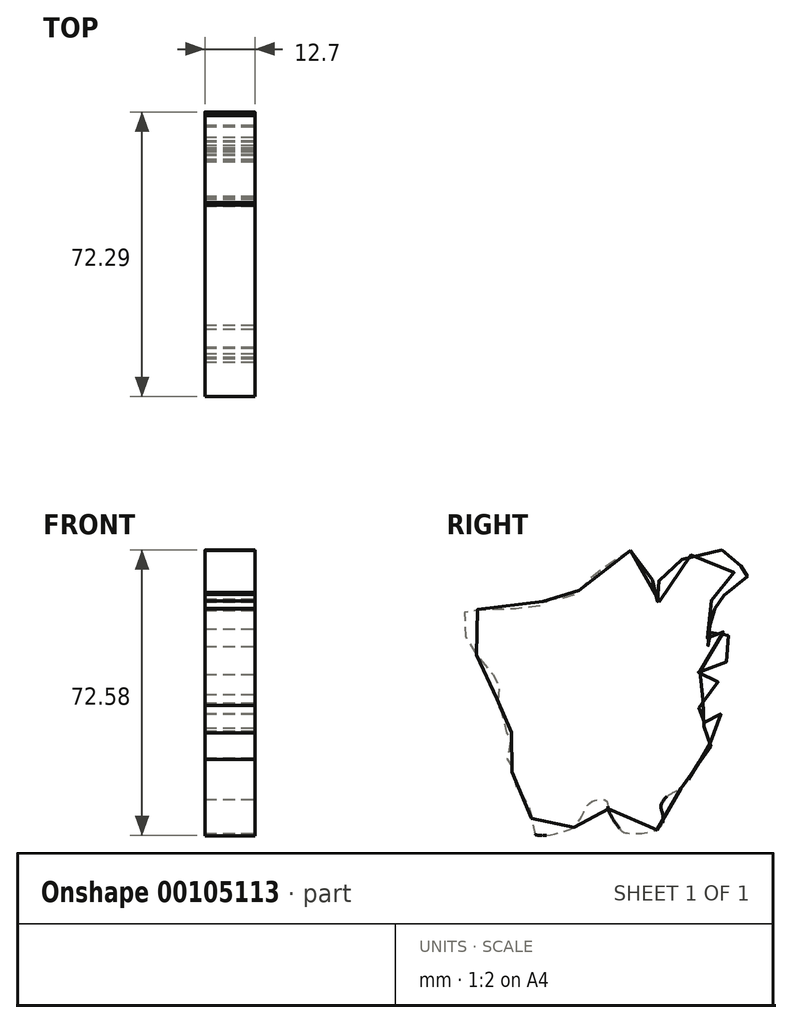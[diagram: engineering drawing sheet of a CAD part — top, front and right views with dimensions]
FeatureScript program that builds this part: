
annotation { "Feature Type Name" : "Feature", "Feature Type Description" : "" }
export const myFeature = defineFeature(function(context is Context, id is Id, definition is map)
    precondition{}
    {
        {
            var Q0;
            Q0=qCreatedBy(makeId("Front.planeOp"),FACE);
            var sketch = newSketch(context, id + "F0", { "sketchPlane" : qUnion([Q0])});
            skLineSegment(sketch, "E0.bottom", {"start": v(38.1, -38.1) * mm, "end": v(-38.1, -38.1) * mm});
            skLineSegment(sketch, "E0.top", {"start": v(38.1, 38.1) * mm, "end": v(-38.1, 38.1) * mm});
            skLineSegment(sketch, "E0.left", {"start": v(38.1, -38.1) * mm, "end": v(38.1, 38.1) * mm});
            skLineSegment(sketch, "E0.right", {"start": v(-38.1, -38.1) * mm, "end": v(-38.1, 38.1) * mm});
            skPoint(sketch, "E0.middle", {"position": v(0, 0) * mm});
            skSolve(sketch);
        }
        {
            var Q0;
            Q0 = qSketchRegion(id + "F0", true);
            extrude(context, id + "F1", {"entities" : qUnion([Q0]), "depth" : 76.2 * mm});
        }
        {
            var Q0;
            Q0=makeQuery(id+"F1.opExtrude","SWEPT_FACE",FACE,{"disambiguationData":[OSD([sQuery(id+"F0.wireOp",EDGE,"E0.right")])]});
            var sketch = newSketch(context, id + "F2", { "sketchPlane" : qUnion([Q0])});
            skFitSpline(sketch, "E1", {"points": [v(30.59, 35.1) * mm, v(34.56, 32.84) * mm, v(38.21, 29.84) * mm, v(41.59, 27.34) * mm, v(44.82, 23.88) * mm, v(45.2, 24.48) * mm, v(48.38, 22.77) * mm, v(48.98, 23.92) * mm, v(51.7, 22.12) * mm, v(53.14, 22.17) * mm, v(54.25, 20.32) * mm, v(60.77, 20.32) * mm, v(69.04, 20.04) * mm, v(72.27, 19.95) * mm, v(73.15, 15.6) * mm, v(71.54, 11.35) * mm, v(69.27, 7.93) * mm, v(65.39, 3.45) * mm, v(63.63, 2.52) * mm, v(64.19, 0) * mm, v(64.51, -2.14) * mm, v(63.9, -4.22) * mm, v(63.26, -3.9) * mm, v(63.54, -8.38) * mm, v(62.2, -11.25) * mm, v(61.18, -10.74) * mm, v(60.72, -12.17) * mm, v(61.78, -13.7) * mm, v(61.78, -17.9) * mm, v(60.67, -17.67) * mm, v(60.81, -18.92) * mm, v(60.35, -22.9) * mm, v(59.01, -26.08) * mm, v(56.51, -29.64) * mm, v(55.13, -31.3) * mm, v(55.82, -33.39) * mm, v(55.73, -36.3) * mm, v(53.05, -37.36) * mm, v(47.46, -36.3) * mm, v(44.5, -34.77) * mm, v(41.96, -30.43) * mm, v(39.74, -28.44) * mm, v(36.69, -28.49) * mm, v(36.22, -30.66) * mm, v(33.68, -35.14) * mm, v(32.2, -36.53) * mm, v(27.44, -36.71) * mm, v(23.1, -35.33) * mm, v(22.36, -32.23) * mm, v(22.82, -29.92) * mm, v(21.16, -27.29) * mm, v(17.55, -25.16) * mm, v(15.38, -21.83) * mm, v(14.6, -19.3) * mm, v(13.8, -19.1) * mm, v(10.02, -15.18) * mm, v(10.48, -14.2) * mm, v(8.12, -10.5) * mm, v(7.75, -6.44) * mm, v(11.82, -10) * mm, v(11.68, -8.2) * mm, v(12.38, -6.35) * mm, v(13.35, -6.26) * mm, v(12.98, -2.98) * mm, v(13.53, -1.45) * mm, v(10.94, -3.62) * mm, v(8.36, -0.94) * mm, v(9.6, 3.26) * mm, v(13.49, 3.73) * mm, v(12.24, 4.74) * mm, v(7.06, 6.13) * mm, v(4.7, 10.1) * mm, v(5.72, 13.43) * mm, v(9.14, 15.14) * mm, v(10.39, 14.63) * mm, v(9.51, 13.3) * mm, v(9.79, 11.12) * mm, v(10.8, 10.75) * mm, v(11.04, 13.06) * mm, v(10.76, 15.93) * mm, v(9.6, 16.48) * mm, v(8.5, 18.52) * mm, v(9.23, 20.5) * mm, v(10.16, 22.21) * mm, v(7.57, 23.5) * mm, v(2.72, 25.77) * mm, v(1.15, 28.87) * mm, v(4.29, 29.47) * mm, v(1.98, 31.87) * mm, v(3.78, 34.46) * mm, v(12.42, 34.74) * mm, v(19.26, 31.78) * mm, v(22.91, 28.22) * mm, v(23.88, 24.39) * mm, v(23.2, 22.17) * mm, v(24.72, 22.58) * mm, v(24.62, 23.78) * mm, v(26.01, 30.35) * mm, v(30.59, 35.1) * mm]});
            skSolve(sketch);
        }
        {
            var Q0;
            Q0 = qSketchRegion(id + "F2", true);
            extrude(context, id + "F3", {"entities" : qUnion([Q0]), "operationType" : NewBodyOperationType.ADD, "depth" : 12.7 * mm});
        }
        {
            var Q0;
            Q0=makeQuery(id+"F1.opExtrude","CAP_FACE",FACE,{"disambiguationData":[OSD([sQuery(id+"F0.wireOp",EDGE,"E0.bottom"),sQuery(id+"F0.wireOp",EDGE,"E0.top"),sQuery(id+"F0.wireOp",EDGE,"E0.left"),sQuery(id+"F0.wireOp",EDGE,"E0.right")])],"isStart":true});
            var sketch = newSketch(context, id + "F4", { "sketchPlane" : qUnion([Q0])});
            skSolve(sketch);
        }
        {
            var Q0;
            Q0=makeQuery(id+"F4.imprint","IMPRINT",FACE,{"disambiguationData":[TD([[makeQuery(id+"F4.imprint","IMPRINT",EDGE,{"derivedFrom":makeQuery(id+"F1.opExtrude","CAP_EDGE",EDGE,{"disambiguationData":[OSD([sQuery(id+"F0.wireOp",EDGE,"E0.bottom")])],"isStart":true})}),1.0]])]});
            extrude(context, id + "F5", {"entities" : qUnion([Q0]), "operationType" : NewBodyOperationType.REMOVE, "oppositeDirection" : true, "depth" : 108.7 * mm});
        }
        {
            var Q0;
            Q0=makeQuery(id+"F3.opExtrude","CAP_FACE",FACE,{"disambiguationData":[OSD([sQuery(id+"F2.wireOp",EDGE,"E1")])],"isStart":false});
            var sketch = newSketch(context, id + "F6", { "sketchPlane" : qUnion([Q0])});
            skFitSpline(sketch, "E2", {"points": [v(26.42, 15.04) * mm, v(26, 17.26) * mm, v(25.8, 20.56) * mm, v(25.92, 24.06) * mm, v(27.03, 27.97) * mm, v(28.72, 31.51) * mm, v(29.71, 32.75) * mm, v(29.46, 31.68) * mm, v(28.19, 29.12) * mm, v(27.57, 26.86) * mm, v(27.16, 24.55) * mm, v(26.91, 20.19) * mm, v(27.2, 15.99) * mm, v(27.32, 14.14) * mm, v(26.42, 15.04) * mm]});
            skFitSpline(sketch, "E3", {"points": [v(28.68, 21.1) * mm, v(28.35, 19.9) * mm, v(28.6, 18.13) * mm, v(29.71, 17.51) * mm, v(29.5, 17.96) * mm, v(29.13, 18.75) * mm, v(28.68, 21.1) * mm]});
            skFitSpline(sketch, "E4", {"points": [v(30.04, 18.87) * mm, v(30.53, 19.12) * mm, v(30.74, 18.46) * mm, v(30.04, 18.87) * mm]});
            skFitSpline(sketch, "E5", {"points": [v(30.99, 19.65) * mm, v(31.81, 19.57) * mm, v(31.77, 19.12) * mm, v(30.99, 19.65) * mm]});
            skFitSpline(sketch, "E6", {"points": [v(31.52, 20.8) * mm, v(32.3, 20.85) * mm, v(32.84, 20.02) * mm, v(32.96, 18.87) * mm, v(32.35, 19.16) * mm, v(31.52, 20.8) * mm]});
            skFitSpline(sketch, "E7", {"points": [v(32.55, 27.02) * mm, v(33.21, 24.22) * mm, v(33.33, 22) * mm, v(33.21, 20.1) * mm, v(33.87, 20.8) * mm, v(34.12, 23.69) * mm, v(33.62, 26.08) * mm, v(32.55, 27.02) * mm]});
            skFitSpline(sketch, "E8", {"points": [v(30.53, 33.49) * mm, v(33.83, 31.63) * mm, v(37.9, 28.3) * mm, v(37.74, 28.83) * mm, v(40.3, 26.82) * mm, v(43.46, 23.65) * mm, v(44.66, 22.45) * mm, v(45.77, 22.2) * mm, v(49.56, 20.44) * mm, v(50.1, 20.1) * mm, v(49.93, 20.52) * mm, v(51.16, 20.19) * mm, v(51.74, 19.57) * mm, v(51.99, 20.06) * mm, v(52.93, 19.57) * mm, v(53.43, 18.09) * mm, v(53.92, 18.3) * mm, v(56.4, 18.66) * mm, v(58.41, 18.58) * mm, v(58.95, 18.75) * mm, v(62.57, 19.28) * mm, v(66.4, 19.28) * mm, v(69.53, 19.12) * mm, v(69.2, 18.7) * mm, v(70.4, 18.7) * mm, v(70.72, 19.28) * mm, v(70.84, 18.46) * mm, v(71.87, 17.76) * mm, v(71.7, 15.82) * mm, v(70.97, 13.35) * mm, v(69.44, 10.47) * mm, v(67.6, 7.26) * mm, v(64.92, 4.5) * mm, v(62.36, 2.77) * mm, v(61.79, 3.27) * mm, v(62, 3.8) * mm, v(65.78, 7.14) * mm, v(68.37, 11.17) * mm, v(70.27, 16.07) * mm, v(70.19, 17.64) * mm, v(66.4, 17.72) * mm, v(61.5, 17.51) * mm, v(56.6, 16.9) * mm, v(54.21, 16.6) * mm, v(54.83, 17.35) * mm, v(55, 17.55) * mm, v(53.06, 17.39) * mm, v(52.48, 18.62) * mm, v(51.9, 17.84) * mm, v(51.08, 18.3) * mm, v(50.75, 18.95) * mm, v(48.49, 20.27) * mm, v(45.9, 21.34) * mm, v(45.73, 20.85) * mm, v(44.37, 21.59) * mm, v(42.76, 23.15) * mm, v(41.12, 23.85) * mm, v(37.9, 26.78) * mm, v(35.31, 29.04) * mm, v(32.68, 31.02) * mm, v(30.53, 33.49) * mm]});
            skFitSpline(sketch, "E9", {"points": [v(60.26, 8.37) * mm, v(60.06, 10.22) * mm, v(61.2, 12.45) * mm, v(64.05, 13.93) * mm, v(66.15, 14.71) * mm, v(68.05, 14.67) * mm, v(66.69, 14.22) * mm, v(63.15, 12.4) * mm, v(61.25, 10.6) * mm, v(60.26, 8.37) * mm]});
            skFitSpline(sketch, "E10", {"points": [v(61.09, 8.58) * mm, v(62.03, 8.87) * mm, v(62.28, 8.5) * mm, v(61.95, 8.08) * mm, v(62.24, 7.8) * mm, v(61.75, 7.05) * mm, v(62.12, 6.72) * mm, v(60.84, 6.64) * mm, v(61.13, 6.85) * mm, v(61.42, 7.3) * mm, v(61.09, 7.75) * mm, v(61.42, 7.84) * mm, v(61.09, 8.58) * mm]});
            skFitSpline(sketch, "E11", {"points": [v(61.79, 2.44) * mm, v(62.45, 1.5) * mm, v(62.73, -0.6) * mm, v(62.9, -2.91) * mm, v(62.36, -2.58) * mm, v(62.2, -3.08) * mm, v(62.12, -4.15) * mm, v(62.28, -6.37) * mm, v(62.24, -8.18) * mm, v(61.79, -9.66) * mm, v(61.79, -8.26) * mm, v(61.37, -5.96) * mm, v(61, -6.95) * mm, v(61.05, -9.09) * mm, v(60.47, -10.98) * mm, v(60.02, -10.53) * mm, v(59.32, -11.43) * mm, v(59.65, -9.38) * mm, v(60.1, -8.6) * mm, v(60.26, -9.17) * mm, v(60.26, -8.02) * mm, v(60.6, -7.03) * mm, v(61.09, -5.34) * mm, v(61.79, -2.25) * mm, v(61.79, 2.44) * mm]});
            skFitSpline(sketch, "E12", {"points": [v(58.53, -10.86) * mm, v(58.62, -11.85) * mm, v(57.8, -12.1) * mm, v(58.29, -11.48) * mm, v(56.56, -12.59) * mm, v(54.05, -13.5) * mm, v(52.56, -13.7) * mm, v(52.15, -14.15) * mm, v(51.04, -14.23) * mm, v(51.37, -13.7) * mm, v(51.12, -13.53) * mm, v(53.14, -13.08) * mm, v(55.82, -12.67) * mm, v(58.53, -10.86) * mm]});
            skFitSpline(sketch, "E13", {"points": [v(46.55, -14.52) * mm, v(49.4, -14.2) * mm, v(49.76, -13.78) * mm, v(50.26, -13.7) * mm, v(50.67, -13.9) * mm, v(50.18, -14.28) * mm, v(49.89, -14.23) * mm, v(49.31, -14.77) * mm, v(46.55, -14.52) * mm]});
            skFitSpline(sketch, "E14", {"points": [v(45.2, -13.29) * mm, v(45.11, -14.2) * mm, v(43.88, -15.8) * mm, v(41.61, -16.3) * mm, v(38.65, -16.42) * mm, v(36.5, -15.72) * mm, v(34.28, -15.22) * mm, v(32.35, -14.4) * mm, v(29.96, -11.97) * mm, v(29.05, -10.03) * mm, v(28.97, -8.92) * mm, v(29.67, -8.39) * mm, v(29.34, -7.11) * mm, v(29.55, -6.66) * mm, v(29.8, -7.6) * mm, v(29.83, -9.54) * mm, v(30.74, -11.31) * mm, v(32.72, -13.25) * mm, v(35.15, -14.6) * mm, v(38.36, -15.47) * mm, v(41.61, -15.51) * mm, v(44.33, -14.52) * mm, v(45.2, -13.29) * mm]});
            skFitSpline(sketch, "E15", {"points": [v(33.91, -11.15) * mm, v(34.82, -10.7) * mm, v(36.8, -10.98) * mm, v(38.9, -11.8) * mm, v(39.51, -12.55) * mm, v(39.35, -13.62) * mm, v(37.78, -13.82) * mm, v(34.86, -12.59) * mm, v(34.03, -11.8) * mm, v(33.91, -11.15) * mm]});
            skFitSpline(sketch, "E16", {"points": [v(33.13, -1.76) * mm, v(33.91, -0.9) * mm, v(34.24, 0.96) * mm, v(34.2, 3.27) * mm, v(33.13, 5.28) * mm, v(31.85, 6.23) * mm, v(29.01, 6.6) * mm, v(27.7, 5.94) * mm, v(27.86, 5.04) * mm, v(27.98, 2.77) * mm, v(28.8, 0) * mm, v(30.78, -0.98) * mm, v(32.6, -1.02) * mm, v(32.6, -1.63) * mm, v(33.13, -1.76) * mm]});
            skFitSpline(sketch, "E17", {"points": [v(47.62, -7.48) * mm, v(47.54, -5.75) * mm, v(48.45, -3.7) * mm, v(50.71, -2.38) * mm, v(53.14, -1.68) * mm, v(55.12, -2.58) * mm, v(55.4, -3.24) * mm, v(55.16, -4.4) * mm, v(53.39, -7.2) * mm, v(50.01, -8.26) * mm, v(48, -7.11) * mm, v(47.62, -7.48) * mm]});
            skFitSpline(sketch, "E18", {"points": [v(31.11, 7.88) * mm, v(29.01, 9.77) * mm, v(27.16, 9.85) * mm, v(26.3, 8.37) * mm, v(25.68, 5.24) * mm, v(25.96, 1.82) * mm, v(27.65, -1.3) * mm, v(30.66, -3.36) * mm, v(31.9, -4.19) * mm, v(31.81, -5.18) * mm, v(33.09, -3.45) * mm, v(32.43, -2.46) * mm, v(29.96, -1.8) * mm, v(27.98, -0.44) * mm, v(27.36, 1.66) * mm, v(27.12, 4.67) * mm, v(27.03, 6.52) * mm, v(28.56, 7.3) * mm, v(31.44, 7.26) * mm, v(31.11, 7.88) * mm]});
            skFitSpline(sketch, "E19", {"points": [v(53.67, -0.85) * mm, v(56.52, 0) * mm, v(59.07, -0.81) * mm, v(58.33, -2.87) * mm, v(56.93, -6.41) * mm, v(53.35, -9.62) * mm, v(48, -10.4) * mm, v(46.26, -10.61) * mm, v(46.22, -8.14) * mm, v(47.42, -8.26) * mm, v(47.3, -9) * mm, v(50.38, -9.3) * mm, v(54.05, -8.06) * mm, v(56.02, -5.34) * mm, v(56.43, -2.79) * mm, v(55.82, -1.76) * mm, v(53.67, -0.85) * mm]});
            skFitSpline(sketch, "E20", {"points": [v(37.25, -9.95) * mm, v(38.93, -10.53) * mm, v(41, -6.37) * mm, v(42.68, -3.24) * mm, v(45.9, -1.3) * mm, v(48.9, 1.58) * mm, v(50.59, 6.89) * mm, v(49.72, 12.2) * mm, v(48.65, 15.37) * mm, v(48.49, 18.42) * mm, v(46.88, 19.16) * mm, v(45.48, 16.81) * mm, v(41.4, 14.26) * mm, v(38.9, 10.18) * mm, v(37.86, 5.65) * mm, v(38.32, 0.34) * mm, v(39.06, -2.79) * mm, v(38.15, -5.18) * mm, v(37.25, -9.95) * mm]});
            skFitSpline(sketch, "E21", {"points": [v(46.63, 14.55) * mm, v(43.26, 12.28) * mm, v(40.33, 7.71) * mm, v(40.13, 1.82) * mm, v(41, -1.14) * mm, v(41.7, -1.06) * mm, v(45.73, 0.8) * mm, v(47.75, 4.83) * mm, v(47.87, 10.84) * mm, v(46.63, 14.55) * mm]});
            skFitSpline(sketch, "E22", {"points": [v(28.29, -9.94) * mm, v(28.45, -8.92) * mm, v(26.1, -6.37) * mm, v(24.75, -5.08) * mm, v(25.28, -6.37) * mm, v(27.1, -9.57) * mm, v(28.29, -9.94) * mm]});
            skFitSpline(sketch, "E23", {"points": [v(25.94, -5.24) * mm, v(25.53, -4.96) * mm, v(25.2, -3.93) * mm, v(25.28, -3.52) * mm, v(25.9, -4.05) * mm, v(25.94, -5.24) * mm]});
            skFitSpline(sketch, "E24", {"points": [v(24.13, -3.3) * mm, v(23.55, -2.32) * mm, v(23.64, -0.39) * mm, v(24, -1.58) * mm, v(24.13, -3.3) * mm]});
            skFitSpline(sketch, "E25", {"points": [v(22.57, 0) * mm, v(22.4, 1.3) * mm, v(22.73, 1.84) * mm, v(22.57, 0) * mm]});
            skFitSpline(sketch, "E26", {"points": [v(21.29, 3.9) * mm, v(21.58, 3.4) * mm, v(21.25, 1.3) * mm, v(21.37, 0.6) * mm, v(20.59, 1.3) * mm, v(21.29, 3.9) * mm]});
            skFitSpline(sketch, "E27", {"points": [v(22.44, 5.83) * mm, v(21.78, 4.8) * mm, v(22.15, 3.94) * mm, v(22.44, 5.83) * mm]});
            skFitSpline(sketch, "E28", {"points": [v(21.82, 5.83) * mm, v(21, 4.64) * mm, v(20.18, 2.5) * mm, v(20.1, 1.88) * mm, v(19.68, 3.6) * mm, v(20.59, 5.83) * mm, v(21.99, 7.4) * mm, v(22.44, 8.63) * mm, v(23.14, 11.02) * mm, v(24.13, 12.54) * mm, v(24.83, 13.28) * mm, v(24.58, 13.5) * mm, v(26.27, 14.64) * mm, v(25.61, 13.08) * mm, v(25.86, 12.46) * mm, v(24.13, 9.41) * mm, v(22.44, 6.37) * mm, v(21.82, 5.83) * mm]});
            skFitSpline(sketch, "E29", {"points": [v(22.42, 16.84) * mm, v(20.84, 17.61) * mm, v(19.88, 19.45) * mm, v(20.77, 21.68) * mm, v(21.57, 24.21) * mm, v(20.32, 27.3) * mm, v(16.07, 30.74) * mm, v(11.92, 32.36) * mm, v(6.57, 33.02) * mm, v(4.11, 32.72) * mm, v(3.05, 32.5) * mm, v(3.93, 33.1) * mm, v(7.08, 33.68) * mm, v(11.26, 33.16) * mm, v(15.34, 31.95) * mm, v(18.78, 29.86) * mm, v(21.24, 27.15) * mm, v(22.27, 24.7) * mm, v(21.72, 21.65) * mm, v(20.8, 19.63) * mm, v(21.02, 18.09) * mm, v(22.42, 16.84) * mm]});
            skFitSpline(sketch, "E30", {"points": [v(14.3, 28.73) * mm, v(16.1, 27.48) * mm, v(18.09, 23.96) * mm, v(18.6, 20.29) * mm, v(17.87, 17.2) * mm, v(17.9, 15.96) * mm, v(17.35, 14.53) * mm, v(15.52, 12.88) * mm, v(12.7, 13.14) * mm, v(11.34, 15.6) * mm, v(11.48, 16.58) * mm, v(11.81, 15.41) * mm, v(14.2, 13.72) * mm, v(15.85, 14.5) * mm, v(16.95, 17.02) * mm, v(15.92, 19.12) * mm, v(14.27, 19.6) * mm, v(13.94, 18.16) * mm, v(15.3, 16.84) * mm, v(14.97, 16.14) * mm, v(13.69, 16.7) * mm, v(12.84, 18.75) * mm, v(13.4, 20.29) * mm, v(15.78, 20.47) * mm, v(16, 21.13) * mm, v(15.19, 23.77) * mm, v(15.15, 24.36) * mm, v(16.03, 23.33) * mm, v(16.8, 20.95) * mm, v(16.47, 20) * mm, v(17.2, 19.67) * mm, v(17.65, 18.93) * mm, v(17.83, 21.57) * mm, v(16.84, 25.13) * mm, v(14.97, 27.88) * mm, v(14.3, 28.73) * mm]});
            skFitSpline(sketch, "E31", {"points": [v(3.12, 28.65) * mm, v(3.49, 27.55) * mm, v(6.97, 25.64) * mm, v(10.27, 24.21) * mm, v(11.89, 22.75) * mm, v(11.85, 20.91) * mm, v(10.1, 19.23) * mm, v(11.45, 19.78) * mm, v(12.88, 21.6) * mm, v(12.14, 24.25) * mm, v(8.95, 25.57) * mm, v(6.46, 26.97) * mm, v(4.62, 27.7) * mm, v(8.33, 27.15) * mm, v(10.5, 28.29) * mm, v(9.14, 30.27) * mm, v(6.39, 31.07) * mm, v(3.82, 32.14) * mm, v(4.3, 31.48) * mm, v(8.51, 29.5) * mm, v(9.65, 28.5) * mm, v(7.78, 27.92) * mm, v(4.62, 28.32) * mm, v(3.12, 28.65) * mm]});
            skFitSpline(sketch, "E32", {"points": [v(11.62, 12.87) * mm, v(13, 10.93) * mm, v(14.88, 9.71) * mm, v(16.2, 9.96) * mm, v(15.43, 10.72) * mm, v(13.18, 12.1) * mm, v(11.62, 12.87) * mm]});
            skFitSpline(sketch, "E33", {"points": [v(25.97, -14.72) * mm, v(25.4, -15.88) * mm, v(25.23, -18.51) * mm, v(26.14, -20.49) * mm, v(26.18, -19.21) * mm, v(26.05, -15.71) * mm, v(25.97, -14.72) * mm]});
            skFitSpline(sketch, "E34", {"points": [v(26.67, -19.3) * mm, v(27.3, -19.66) * mm, v(27.62, -21.27) * mm, v(27.41, -21.76) * mm, v(26.75, -21.31) * mm, v(26.67, -19.3) * mm]});
            skFitSpline(sketch, "E35", {"points": [v(28.2, -21.68) * mm, v(30.67, -23.62) * mm, v(34.25, -25.06) * mm, v(36.55, -26.42) * mm, v(33.14, -25.63) * mm, v(29.97, -24.2) * mm, v(28.2, -21.68) * mm]});
            skFitSpline(sketch, "E36", {"points": [v(36.8, -25.68) * mm, v(38.82, -26.17) * mm, v(39.77, -26.25) * mm, v(38.24, -26.58) * mm, v(36.8, -25.68) * mm]});
            skFitSpline(sketch, "E37", {"points": [v(40.75, -26.13) * mm, v(44.7, -25.26) * mm, v(46.6, -24.85) * mm, v(45.57, -25.76) * mm, v(41.95, -26.46) * mm, v(40.75, -26.13) * mm]});
            skFitSpline(sketch, "E38", {"points": [v(51.91, -24.15) * mm, v(51.79, -22.05) * mm, v(52.98, -18.47) * mm, v(53.85, -17.24) * mm, v(53.19, -19.58) * mm, v(52.74, -23.7) * mm, v(51.91, -24.15) * mm]});
            skFitSpline(sketch, "E39", {"points": [v(18.52, -6.75) * mm, v(19.78, -7.9) * mm, v(21.38, -10.77) * mm, v(21.65, -14.28) * mm, v(21.27, -14.72) * mm, v(21.54, -13.18) * mm, v(19.29, -8.95) * mm, v(18.52, -6.75) * mm]});
            skFitSpline(sketch, "E40", {"points": [v(50.87, -21.87) * mm, v(50.63, -23.3) * mm, v(50.73, -24.13) * mm, v(50.96, -23.62) * mm, v(50.87, -21.87) * mm]});
            skFitSpline(sketch, "E41", {"points": [v(49.8, -23.44) * mm, v(49.66, -24.04) * mm, v(49.94, -24.32) * mm, v(49.8, -23.44) * mm]});
            skFitSpline(sketch, "E42", {"points": [v(59.42, -11.98) * mm, v(60.53, -13.78) * mm, v(60.8, -16.46) * mm, v(60.48, -16.5) * mm, v(59.42, -11.98) * mm]});
            skFitSpline(sketch, "E43", {"points": [v(58.9, -14.47) * mm, v(59.46, -15.17) * mm, v(60.02, -17.02) * mm, v(59.14, -21.91) * mm, v(57.66, -26.03) * mm, v(54.8, -30.56) * mm, v(54.29, -31.8) * mm, v(55.03, -34.2) * mm, v(54.52, -36.1) * mm, v(51.93, -36.2) * mm, v(47.4, -35.18) * mm, v(46.48, -34.35) * mm, v(46.3, -34.67) * mm, v(45.13, -34.25) * mm, v(43.8, -31.2) * mm, v(42.82, -29.12) * mm, v(41.34, -28.06) * mm, v(41.16, -26.9) * mm, v(42.22, -27.65) * mm, v(43.84, -29.08) * mm, v(43.7, -29.59) * mm, v(44.81, -31.43) * mm, v(46.7, -33.84) * mm, v(47.95, -34.8) * mm, v(51.28, -35.6) * mm, v(52.07, -35.6) * mm, v(52.25, -34.76) * mm, v(52.53, -35.5) * mm, v(53.36, -35.32) * mm, v(53.22, -34.8) * mm, v(53.6, -34.62) * mm, v(54.05, -34.8) * mm, v(53.6, -33.2) * mm, v(53.69, -31.02) * mm, v(54.66, -29.45) * mm, v(56, -27.18) * mm, v(57.61, -23.95) * mm, v(58.08, -22.42) * mm, v(57.98, -24.04) * mm, v(58.9, -21.04) * mm, v(59.18, -18.22) * mm, v(59.05, -16.5) * mm, v(59.46, -16.41) * mm, v(58.9, -14.47) * mm]});
            skFitSpline(sketch, "E44", {"points": [v(34.5, -26.63) * mm, v(34.32, -27.88) * mm, v(34.5, -28.38) * mm, v(34.09, -28.75) * mm, v(34.14, -29.5) * mm, v(34.64, -28.94) * mm, v(35.24, -28.66) * mm, v(34.5, -26.63) * mm]});
            skFitSpline(sketch, "E45", {"points": [v(34.64, -30.75) * mm, v(33.94, -32.69) * mm, v(31.72, -35.18) * mm, v(29.4, -35.55) * mm, v(27.33, -35.05) * mm, v(26.91, -35.28) * mm, v(25.99, -34.82) * mm, v(24.5, -34.68) * mm, v(23.58, -32.5) * mm, v(23.58, -30.56) * mm, v(23.81, -31.44) * mm, v(24.04, -30.15) * mm, v(22.75, -27.88) * mm, v(21.46, -25.43) * mm, v(20.35, -23.77) * mm, v(19.33, -19.66) * mm, v(19.15, -16.7) * mm, v(19.24, -13.46) * mm, v(18.04, -10.55) * mm, v(17.2, -10.55) * mm, v(17.25, -12.26) * mm, v(18.31, -13.92) * mm, v(18.64, -13.92) * mm, v(18.45, -14.8) * mm, v(16.56, -13.7) * mm, v(15.82, -10.92) * mm, v(17.16, -9.3) * mm, v(19.52, -10.6) * mm, v(20.07, -13.5) * mm, v(20.62, -13.88) * mm, v(20.86, -15.87) * mm, v(20.35, -14.72) * mm, v(19.98, -16) * mm, v(20.07, -17.44) * mm, v(23.35, -22.34) * mm, v(21.73, -21.69) * mm, v(20.12, -18.69) * mm, v(20.62, -21.04) * mm, v(21.73, -23.82) * mm, v(23.86, -27.28) * mm, v(25.1, -29.6) * mm, v(25.1, -30.29) * mm, v(24.92, -30.05) * mm, v(25.15, -31.12) * mm, v(24.74, -30.93) * mm, v(24.55, -32.13) * mm, v(25.57, -33.47) * mm, v(26.5, -32.78) * mm, v(26.68, -34.21) * mm, v(27.2, -34.52) * mm, v(27.33, -33.9) * mm, v(28.82, -34.56) * mm, v(30.04, -35.04) * mm, v(31.6, -34.48) * mm, v(32.79, -33.39) * mm, v(32.7, -32.9) * mm, v(33.48, -30.81) * mm, v(34.64, -30.07) * mm, v(33.48, -31.95) * mm, v(33.53, -32.86) * mm, v(34.64, -30.75) * mm]});
            skFitSpline(sketch, "E46", {"points": [v(20.88, -25.28) * mm, v(21.05, -25.81) * mm, v(18.2, -24.37) * mm, v(17.42, -22.77) * mm, v(16.44, -21.57) * mm, v(15.4, -18.32) * mm, v(14.83, -18.7) * mm, v(12.9, -17.33) * mm, v(11.41, -15.03) * mm, v(11.41, -14.74) * mm, v(12.32, -14.7) * mm, v(11.2, -13.22) * mm, v(9.48, -10.83) * mm, v(8.49, -9.26) * mm, v(8.7, -8.64) * mm, v(10.05, -10.13) * mm, v(12.15, -12.06) * mm, v(13.1, -12.19) * mm, v(14.34, -12.97) * mm, v(14.75, -14.2) * mm, v(13.06, -12.93) * mm, v(12.03, -12.68) * mm, v(9.31, -9.76) * mm, v(9.23, -9.96) * mm, v(9.97, -10.87) * mm, v(12.03, -13.7) * mm, v(12.85, -14.5) * mm, v(12.28, -15.1) * mm, v(13.02, -16.39) * mm, v(14.67, -18.03) * mm, v(15.16, -17.74) * mm, v(14.34, -15.73) * mm, v(14.13, -16.22) * mm, v(13.43, -15.27) * mm, v(13.92, -14.99) * mm, v(15.08, -15.64) * mm, v(15.9, -18.11) * mm, v(17.22, -21.4) * mm, v(18.58, -23.3) * mm, v(20.88, -25.28) * mm]});
            skFitSpline(sketch, "E47", {"points": [v(14.34, -12.4) * mm, v(13.72, -11.7) * mm, v(12.85, -8.95) * mm, v(13.51, -8.27) * mm, v(14.46, -7.9) * mm, v(14.62, -6.05) * mm, v(14.3, -2.47) * mm, v(15.12, 1.11) * mm, v(15.53, 1.11) * mm, v(15.45, 0) * mm, v(15.24, -2.92) * mm, v(15.4, -5.1) * mm, v(15.28, -7.9) * mm, v(14.75, -8.95) * mm, v(13.35, -8.95) * mm, v(13.55, -10.13) * mm, v(14.34, -12.4) * mm]});
            skFitSpline(sketch, "E48", {"points": [v(18.86, 13.71) * mm, v(20.06, 12.64) * mm, v(19.4, 12.03) * mm, v(17.84, 12.15) * mm, v(17.96, 11.78) * mm, v(19.94, 11.74) * mm, v(20.6, 12.07) * mm, v(20.18, 13.34) * mm, v(18.86, 13.71) * mm]});
            skFitSpline(sketch, "E49", {"points": [v(18.37, 14.66) * mm, v(19.6, 15.07) * mm, v(22.7, 14.87) * mm, v(24.22, 14.5) * mm, v(24.46, 14.41) * mm, v(24.22, 15.24) * mm, v(23.89, 17.05) * mm, v(24.3, 19.23) * mm, v(24.75, 17.7) * mm, v(25.66, 16.3) * mm, v(25.5, 16.97) * mm, v(24.92, 18.32) * mm, v(24.75, 20.34) * mm, v(24.26, 20.1) * mm, v(23.6, 18.24) * mm, v(23.52, 16.27) * mm, v(23.85, 15.03) * mm, v(22.94, 15.2) * mm, v(19.11, 15.44) * mm, v(18.37, 14.66) * mm]});
            skFitSpline(sketch, "E50", {"points": [v(21.17, 9.3) * mm, v(18.62, 9.1) * mm, v(16.97, 9.51) * mm, v(16.72, 10.63) * mm, v(17.88, 11) * mm, v(20.72, 11.4) * mm, v(22.65, 11.16) * mm, v(20.43, 11.04) * mm, v(18.2, 10.58) * mm, v(17.5, 10.17) * mm, v(19.03, 9.39) * mm, v(21.17, 9.3) * mm]});
            skFitSpline(sketch, "E51", {"points": [v(19.69, 6.71) * mm, v(17.75, 7.83) * mm, v(14.34, 7.87) * mm, v(11.5, 8.03) * mm, v(7.83, 9.84) * mm, v(6.64, 11.49) * mm, v(6.76, 13.22) * mm, v(8.24, 13.59) * mm, v(7.17, 13.05) * mm, v(7.05, 11.53) * mm, v(9.27, 9.3) * mm, v(11.62, 8.53) * mm, v(14.7, 8.15) * mm, v(17.75, 8.11) * mm, v(19.69, 6.71) * mm]});
            skFitSpline(sketch, "E52", {"points": [v(12.4, 0.42) * mm, v(13.4, 1.05) * mm, v(14.77, 1.43) * mm, v(16.03, 1.6) * mm, v(17.6, 1.02) * mm, v(17.6, 0) * mm, v(16.83, -0.43) * mm, v(17.24, -0.68) * mm, v(17.7, -0.4) * mm, v(18.1, 0.58) * mm, v(17.32, 1.6) * mm, v(15.6, 1.93) * mm, v(13.64, 1.46) * mm, v(12.4, 0.42) * mm]});
            skFitSpline(sketch, "E53", {"points": [v(11.11, -0.6) * mm, v(10.7, 0.22) * mm, v(11.28, 1.27) * mm, v(13.28, 2.5) * mm, v(14.74, 2.5) * mm, v(16.17, 2.95) * mm, v(16.17, 4.35) * mm, v(14.57, 5.28) * mm, v(12.65, 6.1) * mm, v(9.99, 6.99) * mm, v(7.98, 7.84) * mm, v(6.66, 9.38) * mm, v(6.52, 10.7) * mm, v(6.47, 11.22) * mm, v(6.33, 10.53) * mm, v(6.69, 8.6) * mm, v(8.17, 7.4) * mm, v(10.18, 6.68) * mm, v(12.24, 6) * mm, v(14.4, 5.09) * mm, v(15.95, 3.9) * mm, v(16, 3.17) * mm, v(14.8, 2.7) * mm, v(12.38, 2.78) * mm, v(10.31, 1.27) * mm, v(10.26, 0) * mm, v(10.34, -0.6) * mm, v(11.11, -0.6) * mm]});
            skFitSpline(sketch, "E54", {"points": [v(16.02, 1.13) * mm, v(16.35, 1.1) * mm, v(16.4, -0.43) * mm, v(17.24, -2.08) * mm, v(17.73, -3.53) * mm, v(17.7, -2.34) * mm, v(18.46, -1.93) * mm, v(19.78, -3.56) * mm, v(20.63, -5.3) * mm, v(20.45, -5.58) * mm, v(19.96, -4.78) * mm, v(19.03, -3.33) * mm, v(18.46, -2.7) * mm, v(18.53, -3.61) * mm, v(18.38, -4.55) * mm, v(17.5, -3.95) * mm, v(16.38, -2.03) * mm, v(15.81, -0.43) * mm, v(16.02, 1.13) * mm]});
            skFitSpline(sketch, "E55", {"points": [v(20.27, -1.04) * mm, v(19.65, -1.95) * mm, v(18.01, -1.67) * mm, v(17.13, -1.1) * mm, v(17.94, -1.36) * mm, v(19.29, -1.51) * mm, v(19.96, -0.45) * mm, v(20.97, -1.04) * mm, v(21.8, -2.76) * mm, v(21.46, -4.2) * mm, v(22.04, -3.98) * mm, v(22.06, -2.24) * mm, v(21.9, -1.72) * mm, v(22.87, -3) * mm, v(22.11, -4.5) * mm, v(21.05, -4.57) * mm, v(21.02, -3.7) * mm, v(21.08, -1.93) * mm, v(20.27, -1.04) * mm]});
            skSolve(sketch);
        }
        {
            var Q0;
            Q0 = qSketchRegion(id + "F6", true);
            var Q1;
            Q1=sQuery(id+"F6.wireOp",EDGE,"E20");
            var Q2;
            Q2=sQuery(id+"F6.wireOp",EDGE,"E21");
            var Q3;
            Q3=sQuery(id+"F6.wireOp",EDGE,"E8");
            var Q4;
            Q4=sQuery(id+"F6.wireOp",EDGE,"E7");
            var Q5;
            Q5=sQuery(id+"F6.wireOp",EDGE,"E6");
            var Q6;
            Q6=sQuery(id+"F6.wireOp",EDGE,"E5");
            var Q7;
            Q7=sQuery(id+"F6.wireOp",EDGE,"E4");
            var Q8;
            Q8=sQuery(id+"F6.wireOp",EDGE,"E3");
            var Q9;
            Q9=sQuery(id+"F6.wireOp",EDGE,"E2");
            var Q10;
            Q10=sQuery(id+"F6.wireOp",EDGE,"E49");
            var Q11;
            Q11=sQuery(id+"F6.wireOp",EDGE,"E28");
            var Q12;
            Q12=sQuery(id+"F6.wireOp",EDGE,"E18");
            var Q13;
            Q13=sQuery(id+"F6.wireOp",EDGE,"E16");
            var Q14;
            Q14=sQuery(id+"F6.wireOp",EDGE,"E17");
            var Q15;
            Q15=sQuery(id+"F6.wireOp",EDGE,"E19");
            var Q16;
            Q16=sQuery(id+"F6.wireOp",EDGE,"E11");
            var Q17;
            Q17=sQuery(id+"F6.wireOp",EDGE,"E9");
            var Q18;
            Q18=sQuery(id+"F6.wireOp",EDGE,"E10");
            var Q19;
            Q19=sQuery(id+"F6.wireOp",EDGE,"E15");
            var Q20;
            Q20=sQuery(id+"F6.wireOp",EDGE,"E14");
            var Q21;
            Q21=sQuery(id+"F6.wireOp",EDGE,"E13");
            var Q22;
            Q22=sQuery(id+"F6.wireOp",EDGE,"E12");
            var Q23;
            Q23=sQuery(id+"F6.wireOp",EDGE,"E42");
            var Q24;
            Q24=sQuery(id+"F6.wireOp",EDGE,"E43");
            var Q25;
            Q25=sQuery(id+"F6.wireOp",EDGE,"E38");
            var Q26;
            Q26=sQuery(id+"F6.wireOp",EDGE,"E40");
            var Q27;
            Q27=sQuery(id+"F6.wireOp",EDGE,"E41");
            var Q28;
            Q28=sQuery(id+"F6.wireOp",EDGE,"E37");
            var Q29;
            Q29=sQuery(id+"F6.wireOp",EDGE,"E36");
            var Q30;
            Q30=sQuery(id+"F6.wireOp",EDGE,"E35");
            var Q31;
            Q31=sQuery(id+"F6.wireOp",EDGE,"E34");
            var Q32;
            Q32=sQuery(id+"F6.wireOp",EDGE,"E33");
            var Q33;
            Q33=sQuery(id+"F6.wireOp",EDGE,"E44");
            var Q34;
            Q34=sQuery(id+"F6.wireOp",EDGE,"E45");
            var Q35;
            Q35=sQuery(id+"F6.wireOp",EDGE,"E39");
            var Q36;
            Q36=sQuery(id+"F6.wireOp",EDGE,"E46");
            var Q37;
            Q37=sQuery(id+"F6.wireOp",EDGE,"E47");
            var Q38;
            Q38=sQuery(id+"F6.wireOp",EDGE,"E52");
            var Q39;
            Q39=sQuery(id+"F6.wireOp",EDGE,"E55");
            var Q40;
            Q40=sQuery(id+"F6.wireOp",EDGE,"E54");
            var Q41;
            Q41=sQuery(id+"F6.wireOp",EDGE,"E53");
            var Q42;
            Q42=sQuery(id+"F6.wireOp",EDGE,"E51");
            var Q43;
            Q43=sQuery(id+"F6.wireOp",EDGE,"E50");
            var Q44;
            Q44=sQuery(id+"F6.wireOp",EDGE,"E48");
            var Q45;
            Q45=sQuery(id+"F6.wireOp",EDGE,"E32");
            var Q46;
            Q46=sQuery(id+"F6.wireOp",EDGE,"E30");
            var Q47;
            Q47=sQuery(id+"F6.wireOp",EDGE,"E31");
            var Q48;
            Q48=sQuery(id+"F6.wireOp",EDGE,"E29");
            var Q49;
            Q49=sQuery(id+"F6.wireOp",EDGE,"E23");
            var Q50;
            Q50=sQuery(id+"F6.wireOp",EDGE,"E24");
            var Q51;
            Q51=sQuery(id+"F6.wireOp",EDGE,"E25");
            var Q52;
            Q52=sQuery(id+"F6.wireOp",EDGE,"E26");
            var Q53;
            Q53=sQuery(id+"F6.wireOp",EDGE,"E27");
            extrude(context, id + "F7", {"entities" : qUnion([Q0]), "bodyType" : ToolBodyType.SURFACE, "surfaceEntities" : qUnion([Q1, Q2, Q3, Q4, Q5, Q6, Q7, Q8, Q9, Q10, Q11, Q12, Q13, Q14, Q15, Q16, Q17, Q18, Q19, Q20, Q21, Q22, Q23, Q24, Q25, Q26, Q27, Q28, Q29, Q30, Q31, Q32, Q33, Q34, Q35, Q36, Q37, Q38, Q39, Q40, Q41, Q42, Q43, Q44, Q45, Q46, Q47, Q48, Q49, Q50, Q51, Q52, Q53]), "depth" : 0.5 * mm});
        }
    });
